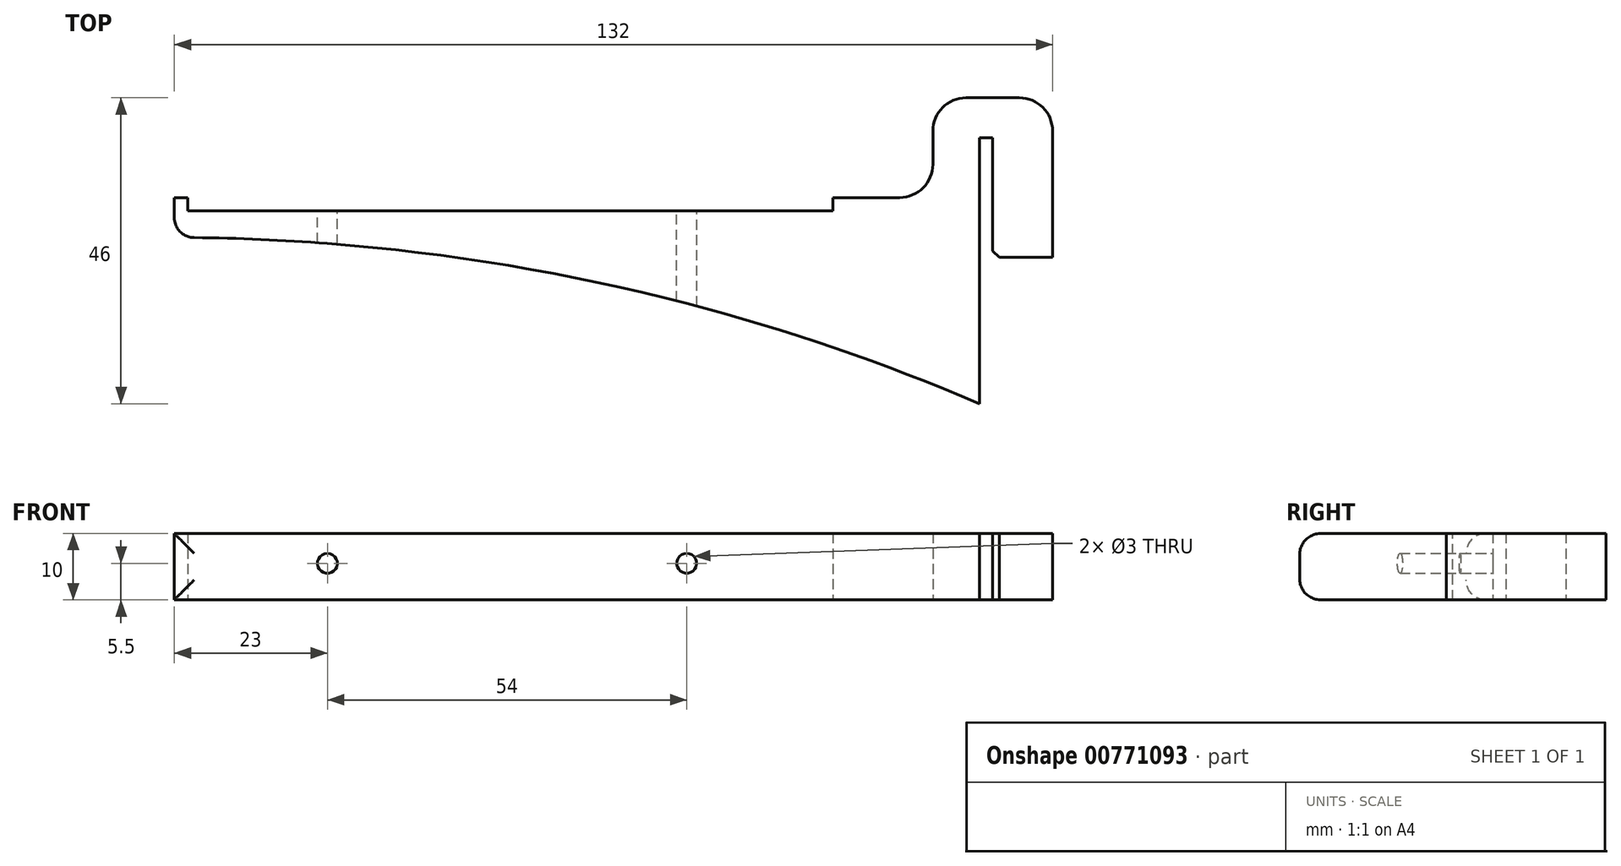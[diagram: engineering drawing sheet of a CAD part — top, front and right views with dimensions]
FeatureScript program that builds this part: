
annotation { "Feature Type Name" : "Feature", "Feature Type Description" : "" }
export const myFeature = defineFeature(function(context is Context, id is Id, definition is map)
    precondition{}
    {
        {
            var Q0;
            Q0=qCreatedBy(makeId("Top.planeOp"),FACE);
            var sketch = newSketch(context, id + "F0", { "sketchPlane" : qUnion([Q0])});
            skLineSegment(sketch, "E0", {"start": v(0, 0) * mm, "end": v(0, 24) * mm});
            skLineSegment(sketch, "E1", {"start": v(0, 0) * mm, "end": v(-9, 0) * mm});
            skLineSegment(sketch, "E2", {"start": v(-9, 0) * mm, "end": v(-9, 18) * mm});
            skLineSegment(sketch, "E3", {"start": v(-9, 18) * mm, "end": v(-11, 18) * mm});
            skLineSegment(sketch, "E4", {"start": v(-11, 18) * mm, "end": v(-11, -22) * mm});
            skLineSegment(sketch, "E5", {"start": v(0, 24) * mm, "end": v(-18, 24) * mm});
            skLineSegment(sketch, "E6", {"start": v(-18, 24) * mm, "end": v(-18, 9) * mm});
            skLineSegment(sketch, "E7", {"start": v(-18, 9) * mm, "end": v(-33, 9) * mm});
            skLineSegment(sketch, "E8", {"start": v(-33, 9) * mm, "end": v(-33, 7) * mm});
            skLineSegment(sketch, "E9", {"start": v(-33, 7) * mm, "end": v(-130, 7) * mm});
            skLineSegment(sketch, "E10", {"start": v(-130, 7) * mm, "end": v(-130, 9) * mm});
            skLineSegment(sketch, "E11", {"start": v(-130, 9) * mm, "end": v(-132, 9) * mm});
            skLineSegment(sketch, "E12", {"start": v(-132, 9) * mm, "end": v(-132, 3) * mm});
            skArc(sketch, "E13", {"start": v(-11, -22) * mm, "mid": v(-70.24, -3.38) * mm, "end": v(-132, 3) * mm});
            skSolve(sketch);
        }
        {
            var Q0;
            Q0 = qSketchRegion(id + "F0", true);
            extrude(context, id + "F1", {"entities" : qUnion([Q0]), "depth" : 10 * mm, "offsetDistance" : 25 * mm});
        }
        {
            var Q0;
            Q0=makeQuery(id+"F1.opExtrude","CAP_EDGE",EDGE,{"disambiguationData":[OSD([sQuery(id+"F0.wireOp",EDGE,"E13")])],"isStart":true});
            var Q1;
            Q1=makeQuery(id+"F1.opExtrude","CAP_EDGE",EDGE,{"disambiguationData":[OSD([sQuery(id+"F0.wireOp",EDGE,"E13")])],"isStart":false});
            var Q2;
            Q2=makeQuery(id+"F1.opExtrude","SWEPT_EDGE",EDGE,{"disambiguationData":[OSD([sQuery(id+"F0.wireOp",EDGE,"E12"),sQuery(id+"F0.wireOp",EDGE,"E13")])]});
            fillet(context, id + "F2", {"entities" : qUnion([Q0, Q1, Q2]), "radius" : 3 * mm, "tangentPropagation" : true, "allowEdgeOverflow" : false});
        }
        {
            var Q0;
            Q0=makeQuery(id+"F1.opExtrude","SWEPT_EDGE",EDGE,{"disambiguationData":[OSD([sQuery(id+"F0.wireOp",EDGE,"E5"),sQuery(id+"F0.wireOp",EDGE,"E6")])]});
            var Q1;
            Q1=makeQuery(id+"F1.opExtrude","SWEPT_EDGE",EDGE,{"disambiguationData":[OSD([sQuery(id+"F0.wireOp",EDGE,"E0"),sQuery(id+"F0.wireOp",EDGE,"E5")])]});
            var Q2;
            Q2=makeQuery(id+"F1.opExtrude","SWEPT_EDGE",EDGE,{"disambiguationData":[OSD([sQuery(id+"F0.wireOp",EDGE,"E6"),sQuery(id+"F0.wireOp",EDGE,"E7")])]});
            fillet(context, id + "F3", {"entities" : qUnion([Q0, Q1, Q2]), "radius" : 5 * mm, "tangentPropagation" : true, "allowEdgeOverflow" : false});
        }
        {
            var Q0;
            Q0=makeQuery(id+"F1.opExtrude","SWEPT_EDGE",EDGE,{"disambiguationData":[OSD([sQuery(id+"F0.wireOp",EDGE,"E1"),sQuery(id+"F0.wireOp",EDGE,"E2")])]});
            chamfer(context, id + "F4", {"entities" : qUnion([Q0]), "width" : 1 * mm, "tangentPropagation" : true});
        }
        {
            var Q0;
            Q0=makeQuery(id+"F1.opExtrude","SWEPT_FACE",FACE,{"disambiguationData":[OSD([sQuery(id+"F0.wireOp",EDGE,"E9")])]});
            var sketch = newSketch(context, id + "F5", { "sketchPlane" : qUnion([Q0])});
            skCircle(sketch, "E14", {"center": v(55, 5.5) * mm, "radius": 1.5 * mm});
            skCircle(sketch, "E15", {"center": v(109, 5.5) * mm, "radius": 1.5 * mm});
            skSolve(sketch);
        }
        {
            var Q0;
            Q0 = qSketchRegion(id + "F5", true);
            extrude(context, id + "F6", {"entities" : qUnion([Q0]), "operationType" : NewBodyOperationType.REMOVE, "oppositeDirection" : true, "depth" : 25 * mm, "offsetDistance" : 25 * mm});
        }
    });
